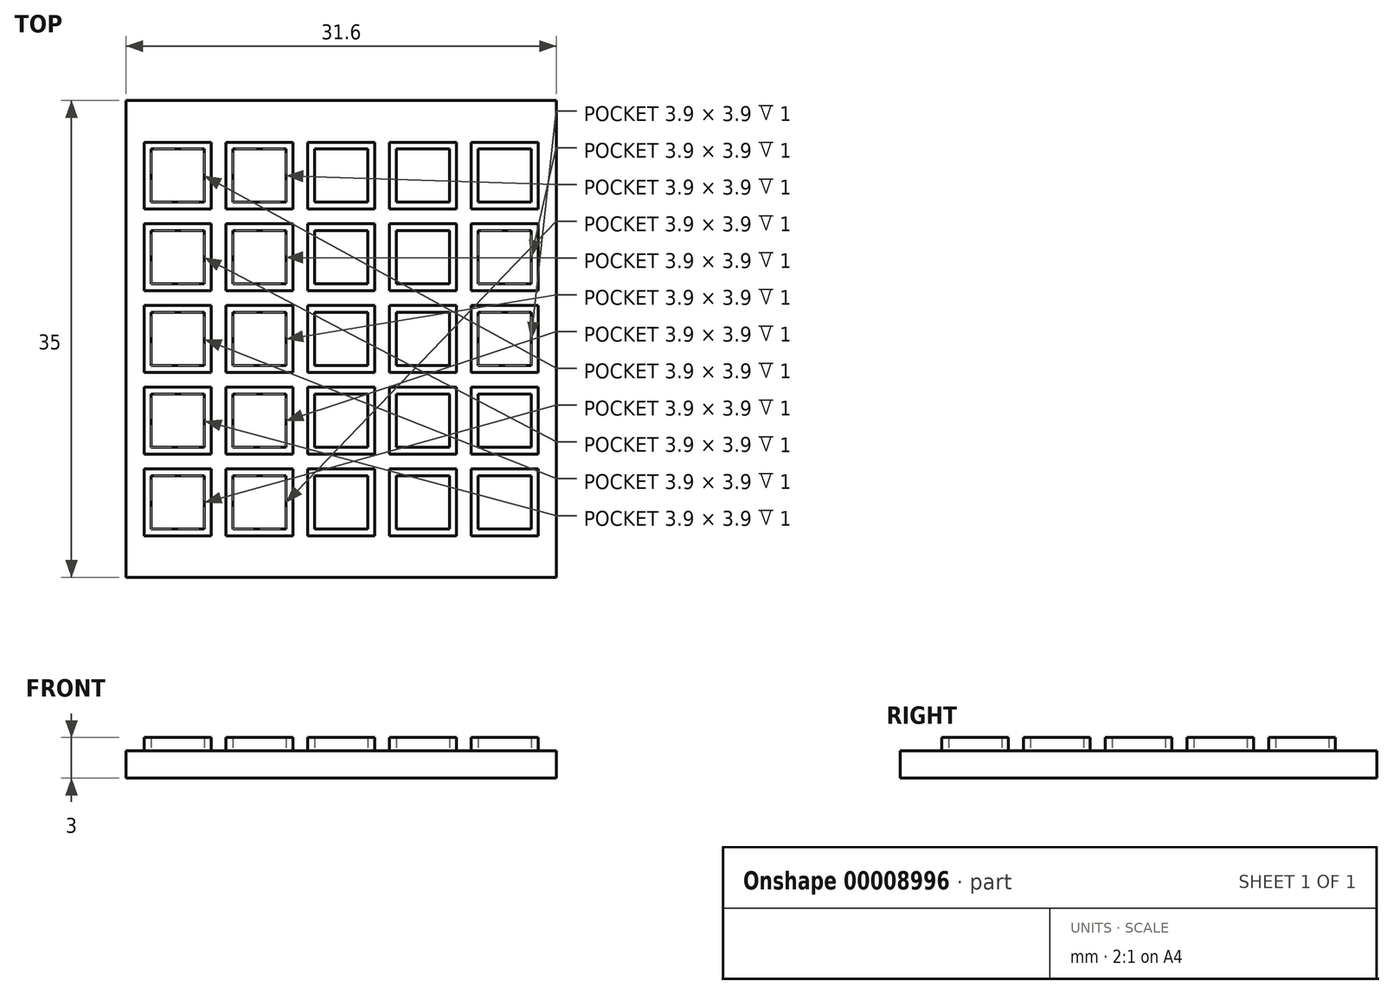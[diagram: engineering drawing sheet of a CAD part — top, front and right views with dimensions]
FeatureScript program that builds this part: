
annotation { "Feature Type Name" : "Feature", "Feature Type Description" : "" }
export const myFeature = defineFeature(function(context is Context, id is Id, definition is map)
    precondition{}
    {
        {
            var Q0;
            Q0=qCreatedBy(makeId("Top.planeOp"),FACE);
            var sketch = newSketch(context, id + "F0", { "sketchPlane" : qUnion([Q0])});
            skLineSegment(sketch, "E0.bottom", {"start": v(0, 0) * mm, "end": v(31.6, 0) * mm});
            skLineSegment(sketch, "E0.top", {"start": v(0, -35) * mm, "end": v(31.6, -35) * mm});
            skLineSegment(sketch, "E0.left", {"start": v(0, 0) * mm, "end": v(0, -35) * mm});
            skLineSegment(sketch, "E0.right", {"start": v(31.6, 0) * mm, "end": v(31.6, -35) * mm});
            skSolve(sketch);
        }
        {
            var Q0;
            Q0 = qSketchRegion(id + "F0", true);
            extrude(context, id + "F1", {"entities" : qUnion([Q0]), "depth" : 2 * mm});
        }
        {
            var Q0;
            Q0=makeQuery(id+"F1.opExtrude","CAP_FACE",FACE,{"disambiguationData":[OSD([sQuery(id+"F0.wireOp",EDGE,"E0.bottom"),sQuery(id+"F0.wireOp",EDGE,"E0.top"),sQuery(id+"F0.wireOp",EDGE,"E0.left"),sQuery(id+"F0.wireOp",EDGE,"E0.right")])],"isStart":false});
            var sketch = newSketch(context, id + "F2", { "sketchPlane" : qUnion([Q0])});
            skLineSegment(sketch, "E1", {"start": v(15.8, 0) * mm, "end": v(15.8, -35) * mm, "construction": true});
            skLineSegment(sketch, "E2.rect.bottom", {"start": v(18.25, -19.95) * mm, "end": v(13.35, -19.95) * mm});
            skLineSegment(sketch, "E2.rect.top", {"start": v(18.25, -15.05) * mm, "end": v(13.35, -15.05) * mm});
            skLineSegment(sketch, "E2.rect.left", {"start": v(18.25, -19.95) * mm, "end": v(18.25, -15.05) * mm});
            skLineSegment(sketch, "E2.rect.right", {"start": v(13.35, -19.95) * mm, "end": v(13.35, -15.05) * mm});
            skPoint(sketch, "E2.rect.middle", {"position": v(15.8, -17.5) * mm});
            skLineSegment(sketch, "E3.rect.bottom", {"start": v(17.75, -19.45) * mm, "end": v(13.85, -19.45) * mm});
            skLineSegment(sketch, "E3.rect.top", {"start": v(17.75, -15.55) * mm, "end": v(13.85, -15.55) * mm});
            skLineSegment(sketch, "E3.rect.left", {"start": v(17.75, -19.45) * mm, "end": v(17.75, -15.55) * mm});
            skLineSegment(sketch, "E3.rect.right", {"start": v(13.85, -19.45) * mm, "end": v(13.85, -15.55) * mm});
            skLineSegment(sketch, "E4.0.1.0", {"start": v(18.25, -13.95) * mm, "end": v(13.35, -13.95) * mm});
            skLineSegment(sketch, "E4.0.1.1", {"start": v(18.25, -9.05) * mm, "end": v(13.35, -9.05) * mm});
            skLineSegment(sketch, "E4.0.1.2", {"start": v(13.85, -13.45) * mm, "end": v(13.85, -9.55) * mm});
            skLineSegment(sketch, "E4.0.1.3", {"start": v(17.75, -13.45) * mm, "end": v(17.75, -9.55) * mm});
            skPoint(sketch, "E4.0.1.4", {"position": v(15.8, -11.5) * mm});
            skLineSegment(sketch, "E4.0.1.5", {"start": v(18.25, -13.95) * mm, "end": v(18.25, -9.05) * mm});
            skLineSegment(sketch, "E4.0.1.6", {"start": v(17.75, -9.55) * mm, "end": v(13.85, -9.55) * mm});
            skLineSegment(sketch, "E4.0.1.7", {"start": v(13.35, -13.95) * mm, "end": v(13.35, -9.05) * mm});
            skLineSegment(sketch, "E4.0.1.8", {"start": v(17.75, -13.45) * mm, "end": v(13.85, -13.45) * mm});
            skPoint(sketch, "E4.0.1.9", {"position": v(15.8, -11.5) * mm});
            skLineSegment(sketch, "E4.0.2.0", {"start": v(18.25, -7.95) * mm, "end": v(13.35, -7.95) * mm});
            skLineSegment(sketch, "E4.0.2.1", {"start": v(18.25, -3.05) * mm, "end": v(13.35, -3.05) * mm});
            skLineSegment(sketch, "E4.0.2.2", {"start": v(13.85, -7.45) * mm, "end": v(13.85, -3.55) * mm});
            skLineSegment(sketch, "E4.0.2.3", {"start": v(17.75, -7.45) * mm, "end": v(17.75, -3.55) * mm});
            skPoint(sketch, "E4.0.2.4", {"position": v(15.8, -5.5) * mm});
            skLineSegment(sketch, "E4.0.2.5", {"start": v(18.25, -7.95) * mm, "end": v(18.25, -3.05) * mm});
            skLineSegment(sketch, "E4.0.2.6", {"start": v(17.75, -3.55) * mm, "end": v(13.85, -3.55) * mm});
            skLineSegment(sketch, "E4.0.2.7", {"start": v(13.35, -7.95) * mm, "end": v(13.35, -3.05) * mm});
            skLineSegment(sketch, "E4.0.2.8", {"start": v(17.75, -7.45) * mm, "end": v(13.85, -7.45) * mm});
            skPoint(sketch, "E4.0.2.9", {"position": v(15.8, -5.5) * mm});
            skLineSegment(sketch, "E4.direction1", {"start": v(13.35, -19.95) * mm, "end": v(38.35, -19.95) * mm, "construction": true});
            skLineSegment(sketch, "E4.direction2", {"start": v(13.35, -19.95) * mm, "end": v(13.35, -13.95) * mm, "construction": true});
            skPoint(sketch, "E5.0.1.0", {"position": v(15.8, -23.5) * mm});
            skLineSegment(sketch, "E5.0.1.1", {"start": v(13.35, -25.95) * mm, "end": v(13.35, -21.05) * mm});
            skLineSegment(sketch, "E5.0.1.2", {"start": v(18.25, -25.95) * mm, "end": v(18.25, -21.05) * mm});
            skLineSegment(sketch, "E5.0.1.3", {"start": v(18.25, -25.95) * mm, "end": v(13.35, -25.95) * mm});
            skLineSegment(sketch, "E5.0.1.4", {"start": v(18.25, -21.05) * mm, "end": v(13.35, -21.05) * mm});
            skLineSegment(sketch, "E5.0.1.5", {"start": v(17.75, -25.45) * mm, "end": v(13.85, -25.45) * mm});
            skLineSegment(sketch, "E5.0.1.6", {"start": v(17.75, -21.55) * mm, "end": v(13.85, -21.55) * mm});
            skLineSegment(sketch, "E5.0.1.7", {"start": v(13.85, -25.45) * mm, "end": v(13.85, -21.55) * mm});
            skPoint(sketch, "E5.0.1.8", {"position": v(15.8, -23.5) * mm});
            skLineSegment(sketch, "E5.0.1.9", {"start": v(17.75, -25.45) * mm, "end": v(17.75, -21.55) * mm});
            skPoint(sketch, "E5.0.2.0", {"position": v(15.8, -29.5) * mm});
            skLineSegment(sketch, "E5.0.2.1", {"start": v(13.35, -31.95) * mm, "end": v(13.35, -27.05) * mm});
            skLineSegment(sketch, "E5.0.2.2", {"start": v(18.25, -31.95) * mm, "end": v(18.25, -27.05) * mm});
            skLineSegment(sketch, "E5.0.2.3", {"start": v(18.25, -31.95) * mm, "end": v(13.35, -31.95) * mm});
            skLineSegment(sketch, "E5.0.2.4", {"start": v(18.25, -27.05) * mm, "end": v(13.35, -27.05) * mm});
            skLineSegment(sketch, "E5.0.2.5", {"start": v(17.75, -31.45) * mm, "end": v(13.85, -31.45) * mm});
            skLineSegment(sketch, "E5.0.2.6", {"start": v(17.75, -27.55) * mm, "end": v(13.85, -27.55) * mm});
            skLineSegment(sketch, "E5.0.2.7", {"start": v(13.85, -31.45) * mm, "end": v(13.85, -27.55) * mm});
            skPoint(sketch, "E5.0.2.8", {"position": v(15.8, -29.5) * mm});
            skLineSegment(sketch, "E5.0.2.9", {"start": v(17.75, -31.45) * mm, "end": v(17.75, -27.55) * mm});
            skLineSegment(sketch, "E5.direction1", {"start": v(15.8, -17.5) * mm, "end": v(40.8, -17.5) * mm, "construction": true});
            skLineSegment(sketch, "E5.direction2", {"start": v(15.8, -17.5) * mm, "end": v(15.8, -23.5) * mm, "construction": true});
            skLineSegment(sketch, "E6.1.0.0", {"start": v(24.25, -31.95) * mm, "end": v(24.25, -27.05) * mm});
            skLineSegment(sketch, "E6.1.0.1", {"start": v(24.25, -25.95) * mm, "end": v(24.25, -21.05) * mm});
            skPoint(sketch, "E6.1.0.2", {"position": v(21.8, -11.5) * mm});
            skPoint(sketch, "E6.1.0.3", {"position": v(21.8, -5.5) * mm});
            skPoint(sketch, "E6.1.0.4", {"position": v(21.8, -29.5) * mm});
            skLineSegment(sketch, "E6.1.0.5", {"start": v(24.25, -7.95) * mm, "end": v(24.25, -3.05) * mm});
            skPoint(sketch, "E6.1.0.6", {"position": v(21.8, -23.5) * mm});
            skPoint(sketch, "E6.1.0.7", {"position": v(21.8, -17.5) * mm});
            skPoint(sketch, "E6.1.0.8", {"position": v(21.8, -5.5) * mm});
            skPoint(sketch, "E6.1.0.9", {"position": v(21.8, -17.5) * mm});
            skPoint(sketch, "E6.1.0.10", {"position": v(21.8, -29.5) * mm});
            skLineSegment(sketch, "E6.1.0.11", {"start": v(21.8, 0) * mm, "end": v(21.8, -35) * mm, "construction": true});
            skPoint(sketch, "E6.1.0.12", {"position": v(21.8, -11.5) * mm});
            skPoint(sketch, "E6.1.0.13", {"position": v(21.8, -23.5) * mm});
            skLineSegment(sketch, "E6.1.0.14", {"start": v(24.25, -25.95) * mm, "end": v(19.35, -25.95) * mm});
            skLineSegment(sketch, "E6.1.0.15", {"start": v(24.25, -31.95) * mm, "end": v(19.35, -31.95) * mm});
            skLineSegment(sketch, "E6.1.0.16", {"start": v(24.25, -7.95) * mm, "end": v(19.35, -7.95) * mm});
            skLineSegment(sketch, "E6.1.0.17", {"start": v(19.35, -31.95) * mm, "end": v(19.35, -27.05) * mm});
            skLineSegment(sketch, "E6.1.0.18", {"start": v(19.85, -7.45) * mm, "end": v(19.85, -3.55) * mm});
            skLineSegment(sketch, "E6.1.0.19", {"start": v(23.75, -31.45) * mm, "end": v(23.75, -27.55) * mm});
            skLineSegment(sketch, "E6.1.0.20", {"start": v(23.75, -7.45) * mm, "end": v(23.75, -3.55) * mm});
            skLineSegment(sketch, "E6.1.0.21", {"start": v(23.75, -25.45) * mm, "end": v(19.85, -25.45) * mm});
            skLineSegment(sketch, "E6.1.0.22", {"start": v(24.25, -3.05) * mm, "end": v(19.35, -3.05) * mm});
            skLineSegment(sketch, "E6.1.0.23", {"start": v(24.25, -19.95) * mm, "end": v(24.25, -15.05) * mm});
            skLineSegment(sketch, "E6.1.0.24", {"start": v(19.85, -31.45) * mm, "end": v(19.85, -27.55) * mm});
            skLineSegment(sketch, "E6.1.0.25", {"start": v(24.25, -27.05) * mm, "end": v(19.35, -27.05) * mm});
            skLineSegment(sketch, "E6.1.0.26", {"start": v(19.35, -7.95) * mm, "end": v(19.35, -3.05) * mm});
            skLineSegment(sketch, "E6.1.0.27", {"start": v(23.75, -31.45) * mm, "end": v(19.85, -31.45) * mm});
            skLineSegment(sketch, "E6.1.0.28", {"start": v(23.75, -3.55) * mm, "end": v(19.85, -3.55) * mm});
            skLineSegment(sketch, "E6.1.0.29", {"start": v(23.75, -27.55) * mm, "end": v(19.85, -27.55) * mm});
            skLineSegment(sketch, "E6.1.0.30", {"start": v(19.85, -25.45) * mm, "end": v(19.85, -21.55) * mm});
            skLineSegment(sketch, "E6.1.0.31", {"start": v(19.35, -25.95) * mm, "end": v(19.35, -21.05) * mm});
            skLineSegment(sketch, "E6.1.0.32", {"start": v(19.85, -13.45) * mm, "end": v(19.85, -9.55) * mm});
            skLineSegment(sketch, "E6.1.0.33", {"start": v(23.75, -13.45) * mm, "end": v(23.75, -9.55) * mm});
            skLineSegment(sketch, "E6.1.0.34", {"start": v(23.75, -19.45) * mm, "end": v(19.85, -19.45) * mm});
            skLineSegment(sketch, "E6.1.0.35", {"start": v(23.75, -15.55) * mm, "end": v(19.85, -15.55) * mm});
            skLineSegment(sketch, "E6.1.0.36", {"start": v(23.75, -19.45) * mm, "end": v(23.75, -15.55) * mm});
            skLineSegment(sketch, "E6.1.0.37", {"start": v(24.25, -9.05) * mm, "end": v(19.35, -9.05) * mm});
            skLineSegment(sketch, "E6.1.0.38", {"start": v(19.85, -19.45) * mm, "end": v(19.85, -15.55) * mm});
            skLineSegment(sketch, "E6.1.0.39", {"start": v(24.25, -13.95) * mm, "end": v(19.35, -13.95) * mm});
            skLineSegment(sketch, "E6.1.0.40", {"start": v(19.35, -19.95) * mm, "end": v(19.35, -15.05) * mm});
            skLineSegment(sketch, "E6.1.0.41", {"start": v(19.35, -19.95) * mm, "end": v(19.35, -13.95) * mm, "construction": true});
            skLineSegment(sketch, "E6.1.0.42", {"start": v(23.75, -25.45) * mm, "end": v(23.75, -21.55) * mm});
            skLineSegment(sketch, "E6.1.0.43", {"start": v(24.25, -19.95) * mm, "end": v(19.35, -19.95) * mm});
            skLineSegment(sketch, "E6.1.0.44", {"start": v(19.35, -13.95) * mm, "end": v(19.35, -9.05) * mm});
            skLineSegment(sketch, "E6.1.0.45", {"start": v(23.75, -9.55) * mm, "end": v(19.85, -9.55) * mm});
            skLineSegment(sketch, "E6.1.0.46", {"start": v(24.25, -13.95) * mm, "end": v(24.25, -9.05) * mm});
            skLineSegment(sketch, "E6.1.0.47", {"start": v(21.8, -17.5) * mm, "end": v(21.8, -23.5) * mm, "construction": true});
            skLineSegment(sketch, "E6.1.0.48", {"start": v(23.75, -21.55) * mm, "end": v(19.85, -21.55) * mm});
            skLineSegment(sketch, "E6.1.0.49", {"start": v(23.75, -13.45) * mm, "end": v(19.85, -13.45) * mm});
            skLineSegment(sketch, "E6.1.0.50", {"start": v(23.75, -7.45) * mm, "end": v(19.85, -7.45) * mm});
            skLineSegment(sketch, "E6.1.0.51", {"start": v(24.25, -21.05) * mm, "end": v(19.35, -21.05) * mm});
            skLineSegment(sketch, "E6.1.0.52", {"start": v(24.25, -15.05) * mm, "end": v(19.35, -15.05) * mm});
            skLineSegment(sketch, "E6.2.0.0", {"start": v(30.25, -31.95) * mm, "end": v(30.25, -27.05) * mm});
            skLineSegment(sketch, "E6.2.0.1", {"start": v(30.25, -25.95) * mm, "end": v(30.25, -21.05) * mm});
            skPoint(sketch, "E6.2.0.2", {"position": v(27.8, -11.5) * mm});
            skPoint(sketch, "E6.2.0.3", {"position": v(27.8, -5.5) * mm});
            skPoint(sketch, "E6.2.0.4", {"position": v(27.8, -29.5) * mm});
            skLineSegment(sketch, "E6.2.0.5", {"start": v(30.25, -7.95) * mm, "end": v(30.25, -3.05) * mm});
            skPoint(sketch, "E6.2.0.6", {"position": v(27.8, -23.5) * mm});
            skPoint(sketch, "E6.2.0.7", {"position": v(27.8, -17.5) * mm});
            skPoint(sketch, "E6.2.0.8", {"position": v(27.8, -5.5) * mm});
            skPoint(sketch, "E6.2.0.9", {"position": v(27.8, -17.5) * mm});
            skPoint(sketch, "E6.2.0.10", {"position": v(27.8, -29.5) * mm});
            skLineSegment(sketch, "E6.2.0.11", {"start": v(27.8, 0) * mm, "end": v(27.8, -35) * mm, "construction": true});
            skPoint(sketch, "E6.2.0.12", {"position": v(27.8, -11.5) * mm});
            skPoint(sketch, "E6.2.0.13", {"position": v(27.8, -23.5) * mm});
            skLineSegment(sketch, "E6.2.0.14", {"start": v(30.25, -25.95) * mm, "end": v(25.35, -25.95) * mm});
            skLineSegment(sketch, "E6.2.0.15", {"start": v(30.25, -31.95) * mm, "end": v(25.35, -31.95) * mm});
            skLineSegment(sketch, "E6.2.0.16", {"start": v(30.25, -7.95) * mm, "end": v(25.35, -7.95) * mm});
            skLineSegment(sketch, "E6.2.0.17", {"start": v(25.35, -31.95) * mm, "end": v(25.35, -27.05) * mm});
            skLineSegment(sketch, "E6.2.0.18", {"start": v(25.85, -7.45) * mm, "end": v(25.85, -3.55) * mm});
            skLineSegment(sketch, "E6.2.0.19", {"start": v(29.75, -31.45) * mm, "end": v(29.75, -27.55) * mm});
            skLineSegment(sketch, "E6.2.0.20", {"start": v(29.75, -7.45) * mm, "end": v(29.75, -3.55) * mm});
            skLineSegment(sketch, "E6.2.0.21", {"start": v(29.75, -25.45) * mm, "end": v(25.85, -25.45) * mm});
            skLineSegment(sketch, "E6.2.0.22", {"start": v(30.25, -3.05) * mm, "end": v(25.35, -3.05) * mm});
            skLineSegment(sketch, "E6.2.0.23", {"start": v(30.25, -19.95) * mm, "end": v(30.25, -15.05) * mm});
            skLineSegment(sketch, "E6.2.0.24", {"start": v(25.85, -31.45) * mm, "end": v(25.85, -27.55) * mm});
            skLineSegment(sketch, "E6.2.0.25", {"start": v(30.25, -27.05) * mm, "end": v(25.35, -27.05) * mm});
            skLineSegment(sketch, "E6.2.0.26", {"start": v(25.35, -7.95) * mm, "end": v(25.35, -3.05) * mm});
            skLineSegment(sketch, "E6.2.0.27", {"start": v(29.75, -31.45) * mm, "end": v(25.85, -31.45) * mm});
            skLineSegment(sketch, "E6.2.0.28", {"start": v(29.75, -3.55) * mm, "end": v(25.85, -3.55) * mm});
            skLineSegment(sketch, "E6.2.0.29", {"start": v(29.75, -27.55) * mm, "end": v(25.85, -27.55) * mm});
            skLineSegment(sketch, "E6.2.0.30", {"start": v(25.85, -25.45) * mm, "end": v(25.85, -21.55) * mm});
            skLineSegment(sketch, "E6.2.0.31", {"start": v(25.35, -25.95) * mm, "end": v(25.35, -21.05) * mm});
            skLineSegment(sketch, "E6.2.0.32", {"start": v(25.85, -13.45) * mm, "end": v(25.85, -9.55) * mm});
            skLineSegment(sketch, "E6.2.0.33", {"start": v(29.75, -13.45) * mm, "end": v(29.75, -9.55) * mm});
            skLineSegment(sketch, "E6.2.0.34", {"start": v(29.75, -19.45) * mm, "end": v(25.85, -19.45) * mm});
            skLineSegment(sketch, "E6.2.0.35", {"start": v(29.75, -15.55) * mm, "end": v(25.85, -15.55) * mm});
            skLineSegment(sketch, "E6.2.0.36", {"start": v(29.75, -19.45) * mm, "end": v(29.75, -15.55) * mm});
            skLineSegment(sketch, "E6.2.0.37", {"start": v(30.25, -9.05) * mm, "end": v(25.35, -9.05) * mm});
            skLineSegment(sketch, "E6.2.0.38", {"start": v(25.85, -19.45) * mm, "end": v(25.85, -15.55) * mm});
            skLineSegment(sketch, "E6.2.0.39", {"start": v(30.25, -13.95) * mm, "end": v(25.35, -13.95) * mm});
            skLineSegment(sketch, "E6.2.0.40", {"start": v(25.35, -19.95) * mm, "end": v(25.35, -15.05) * mm});
            skLineSegment(sketch, "E6.2.0.41", {"start": v(25.35, -19.95) * mm, "end": v(25.35, -13.95) * mm, "construction": true});
            skLineSegment(sketch, "E6.2.0.42", {"start": v(29.75, -25.45) * mm, "end": v(29.75, -21.55) * mm});
            skLineSegment(sketch, "E6.2.0.43", {"start": v(30.25, -19.95) * mm, "end": v(25.35, -19.95) * mm});
            skLineSegment(sketch, "E6.2.0.44", {"start": v(25.35, -13.95) * mm, "end": v(25.35, -9.05) * mm});
            skLineSegment(sketch, "E6.2.0.45", {"start": v(29.75, -9.55) * mm, "end": v(25.85, -9.55) * mm});
            skLineSegment(sketch, "E6.2.0.46", {"start": v(30.25, -13.95) * mm, "end": v(30.25, -9.05) * mm});
            skLineSegment(sketch, "E6.2.0.47", {"start": v(27.8, -17.5) * mm, "end": v(27.8, -23.5) * mm, "construction": true});
            skLineSegment(sketch, "E6.2.0.48", {"start": v(29.75, -21.55) * mm, "end": v(25.85, -21.55) * mm});
            skLineSegment(sketch, "E6.2.0.49", {"start": v(29.75, -13.45) * mm, "end": v(25.85, -13.45) * mm});
            skLineSegment(sketch, "E6.2.0.50", {"start": v(29.75, -7.45) * mm, "end": v(25.85, -7.45) * mm});
            skLineSegment(sketch, "E6.2.0.51", {"start": v(30.25, -21.05) * mm, "end": v(25.35, -21.05) * mm});
            skLineSegment(sketch, "E6.2.0.52", {"start": v(30.25, -15.05) * mm, "end": v(25.35, -15.05) * mm});
            skLineSegment(sketch, "E6.direction1", {"start": v(18.25, -31.95) * mm, "end": v(24.25, -31.95) * mm, "construction": true});
            skPoint(sketch, "E7.1.0.0", {"position": v(9.8, -5.5) * mm});
            skLineSegment(sketch, "E7.1.0.1", {"start": v(7.35, -7.95) * mm, "end": v(7.35, -3.05) * mm});
            skLineSegment(sketch, "E7.1.0.2", {"start": v(12.25, -31.95) * mm, "end": v(12.25, -27.05) * mm});
            skPoint(sketch, "E7.1.0.3", {"position": v(9.8, -11.5) * mm});
            skPoint(sketch, "E7.1.0.4", {"position": v(9.8, -17.5) * mm});
            skPoint(sketch, "E7.1.0.5", {"position": v(9.8, -17.5) * mm});
            skLineSegment(sketch, "E7.1.0.6", {"start": v(12.25, -27.05) * mm, "end": v(7.35, -27.05) * mm});
            skLineSegment(sketch, "E7.1.0.7", {"start": v(12.25, -31.95) * mm, "end": v(7.35, -31.95) * mm});
            skLineSegment(sketch, "E7.1.0.8", {"start": v(12.25, -7.95) * mm, "end": v(12.25, -3.05) * mm});
            skLineSegment(sketch, "E7.1.0.9", {"start": v(12.25, -3.05) * mm, "end": v(7.35, -3.05) * mm});
            skLineSegment(sketch, "E7.1.0.10", {"start": v(12.25, -9.05) * mm, "end": v(7.35, -9.05) * mm});
            skLineSegment(sketch, "E7.1.0.11", {"start": v(12.25, -13.95) * mm, "end": v(7.35, -13.95) * mm});
            skLineSegment(sketch, "E7.1.0.12", {"start": v(7.85, -7.45) * mm, "end": v(7.85, -3.55) * mm});
            skLineSegment(sketch, "E7.1.0.13", {"start": v(7.35, -31.95) * mm, "end": v(7.35, -27.05) * mm});
            skLineSegment(sketch, "E7.1.0.14", {"start": v(12.25, -13.95) * mm, "end": v(12.25, -9.05) * mm});
            skLineSegment(sketch, "E7.1.0.15", {"start": v(11.75, -9.55) * mm, "end": v(7.85, -9.55) * mm});
            skLineSegment(sketch, "E7.1.0.16", {"start": v(7.35, -13.95) * mm, "end": v(7.35, -9.05) * mm});
            skLineSegment(sketch, "E7.1.0.17", {"start": v(9.8, 0) * mm, "end": v(9.8, -35) * mm, "construction": true});
            skLineSegment(sketch, "E7.1.0.18", {"start": v(12.25, -19.95) * mm, "end": v(7.35, -19.95) * mm});
            skLineSegment(sketch, "E7.1.0.19", {"start": v(12.25, -15.05) * mm, "end": v(7.35, -15.05) * mm});
            skLineSegment(sketch, "E7.1.0.20", {"start": v(12.25, -19.95) * mm, "end": v(12.25, -15.05) * mm});
            skLineSegment(sketch, "E7.1.0.21", {"start": v(7.35, -19.95) * mm, "end": v(7.35, -15.05) * mm});
            skLineSegment(sketch, "E7.1.0.22", {"start": v(11.75, -19.45) * mm, "end": v(7.85, -19.45) * mm});
            skLineSegment(sketch, "E7.1.0.23", {"start": v(11.75, -15.55) * mm, "end": v(7.85, -15.55) * mm});
            skLineSegment(sketch, "E7.1.0.24", {"start": v(11.75, -13.45) * mm, "end": v(7.85, -13.45) * mm});
            skPoint(sketch, "E7.1.0.25", {"position": v(9.8, -29.5) * mm});
            skLineSegment(sketch, "E7.1.0.26", {"start": v(12.25, -7.95) * mm, "end": v(7.35, -7.95) * mm});
            skPoint(sketch, "E7.1.0.27", {"position": v(9.8, -29.5) * mm});
            skPoint(sketch, "E7.1.0.28", {"position": v(9.8, -23.5) * mm});
            skLineSegment(sketch, "E7.1.0.29", {"start": v(9.8, -17.5) * mm, "end": v(9.8, -23.5) * mm, "construction": true});
            skLineSegment(sketch, "E7.1.0.30", {"start": v(12.25, -25.95) * mm, "end": v(12.25, -21.05) * mm});
            skPoint(sketch, "E7.1.0.31", {"position": v(9.8, -5.5) * mm});
            skLineSegment(sketch, "E7.1.0.32", {"start": v(12.25, -25.95) * mm, "end": v(7.35, -25.95) * mm});
            skPoint(sketch, "E7.1.0.33", {"position": v(9.8, -23.5) * mm});
            skLineSegment(sketch, "E7.1.0.34", {"start": v(7.35, -25.95) * mm, "end": v(7.35, -21.05) * mm});
            skLineSegment(sketch, "E7.1.0.35", {"start": v(12.25, -21.05) * mm, "end": v(7.35, -21.05) * mm});
            skPoint(sketch, "E7.1.0.36", {"position": v(9.8, -11.5) * mm});
            skLineSegment(sketch, "E7.1.0.37", {"start": v(7.35, -19.95) * mm, "end": v(7.35, -13.95) * mm, "construction": true});
            skLineSegment(sketch, "E7.1.0.38", {"start": v(11.75, -31.45) * mm, "end": v(11.75, -27.55) * mm});
            skLineSegment(sketch, "E7.1.0.39", {"start": v(11.75, -7.45) * mm, "end": v(7.85, -7.45) * mm});
            skLineSegment(sketch, "E7.1.0.40", {"start": v(11.75, -27.55) * mm, "end": v(7.85, -27.55) * mm});
            skLineSegment(sketch, "E7.1.0.41", {"start": v(11.75, -31.45) * mm, "end": v(7.85, -31.45) * mm});
            skLineSegment(sketch, "E7.1.0.42", {"start": v(7.85, -31.45) * mm, "end": v(7.85, -27.55) * mm});
            skLineSegment(sketch, "E7.1.0.43", {"start": v(11.75, -7.45) * mm, "end": v(11.75, -3.55) * mm});
            skLineSegment(sketch, "E7.1.0.44", {"start": v(11.75, -3.55) * mm, "end": v(7.85, -3.55) * mm});
            skLineSegment(sketch, "E7.1.0.45", {"start": v(11.75, -25.45) * mm, "end": v(11.75, -21.55) * mm});
            skLineSegment(sketch, "E7.1.0.46", {"start": v(11.75, -13.45) * mm, "end": v(11.75, -9.55) * mm});
            skLineSegment(sketch, "E7.1.0.47", {"start": v(7.85, -13.45) * mm, "end": v(7.85, -9.55) * mm});
            skLineSegment(sketch, "E7.1.0.48", {"start": v(7.85, -19.45) * mm, "end": v(7.85, -15.55) * mm});
            skLineSegment(sketch, "E7.1.0.49", {"start": v(11.75, -19.45) * mm, "end": v(11.75, -15.55) * mm});
            skLineSegment(sketch, "E7.1.0.50", {"start": v(11.75, -21.55) * mm, "end": v(7.85, -21.55) * mm});
            skLineSegment(sketch, "E7.1.0.51", {"start": v(7.85, -25.45) * mm, "end": v(7.85, -21.55) * mm});
            skLineSegment(sketch, "E7.1.0.52", {"start": v(11.75, -25.45) * mm, "end": v(7.85, -25.45) * mm});
            skPoint(sketch, "E7.2.0.0", {"position": v(3.8, -5.5) * mm});
            skLineSegment(sketch, "E7.2.0.1", {"start": v(1.35, -7.95) * mm, "end": v(1.35, -3.05) * mm});
            skLineSegment(sketch, "E7.2.0.2", {"start": v(6.25, -31.95) * mm, "end": v(6.25, -27.05) * mm});
            skPoint(sketch, "E7.2.0.3", {"position": v(3.8, -11.5) * mm});
            skPoint(sketch, "E7.2.0.4", {"position": v(3.8, -17.5) * mm});
            skPoint(sketch, "E7.2.0.5", {"position": v(3.8, -17.5) * mm});
            skLineSegment(sketch, "E7.2.0.6", {"start": v(6.25, -27.05) * mm, "end": v(1.35, -27.05) * mm});
            skLineSegment(sketch, "E7.2.0.7", {"start": v(6.25, -31.95) * mm, "end": v(1.35, -31.95) * mm});
            skLineSegment(sketch, "E7.2.0.8", {"start": v(6.25, -7.95) * mm, "end": v(6.25, -3.05) * mm});
            skLineSegment(sketch, "E7.2.0.9", {"start": v(6.25, -3.05) * mm, "end": v(1.35, -3.05) * mm});
            skLineSegment(sketch, "E7.2.0.10", {"start": v(6.25, -9.05) * mm, "end": v(1.35, -9.05) * mm});
            skLineSegment(sketch, "E7.2.0.11", {"start": v(6.25, -13.95) * mm, "end": v(1.35, -13.95) * mm});
            skLineSegment(sketch, "E7.2.0.12", {"start": v(1.85, -7.45) * mm, "end": v(1.85, -3.55) * mm});
            skLineSegment(sketch, "E7.2.0.13", {"start": v(1.35, -31.95) * mm, "end": v(1.35, -27.05) * mm});
            skLineSegment(sketch, "E7.2.0.14", {"start": v(6.25, -13.95) * mm, "end": v(6.25, -9.05) * mm});
            skLineSegment(sketch, "E7.2.0.15", {"start": v(5.75, -9.55) * mm, "end": v(1.85, -9.55) * mm});
            skLineSegment(sketch, "E7.2.0.16", {"start": v(1.35, -13.95) * mm, "end": v(1.35, -9.05) * mm});
            skLineSegment(sketch, "E7.2.0.17", {"start": v(3.8, 0) * mm, "end": v(3.8, -35) * mm, "construction": true});
            skLineSegment(sketch, "E7.2.0.18", {"start": v(6.25, -19.95) * mm, "end": v(1.35, -19.95) * mm});
            skLineSegment(sketch, "E7.2.0.19", {"start": v(6.25, -15.05) * mm, "end": v(1.35, -15.05) * mm});
            skLineSegment(sketch, "E7.2.0.20", {"start": v(6.25, -19.95) * mm, "end": v(6.25, -15.05) * mm});
            skLineSegment(sketch, "E7.2.0.21", {"start": v(1.35, -19.95) * mm, "end": v(1.35, -15.05) * mm});
            skLineSegment(sketch, "E7.2.0.22", {"start": v(5.75, -19.45) * mm, "end": v(1.85, -19.45) * mm});
            skLineSegment(sketch, "E7.2.0.23", {"start": v(5.75, -15.55) * mm, "end": v(1.85, -15.55) * mm});
            skLineSegment(sketch, "E7.2.0.24", {"start": v(5.75, -13.45) * mm, "end": v(1.85, -13.45) * mm});
            skPoint(sketch, "E7.2.0.25", {"position": v(3.8, -29.5) * mm});
            skLineSegment(sketch, "E7.2.0.26", {"start": v(6.25, -7.95) * mm, "end": v(1.35, -7.95) * mm});
            skPoint(sketch, "E7.2.0.27", {"position": v(3.8, -29.5) * mm});
            skPoint(sketch, "E7.2.0.28", {"position": v(3.8, -23.5) * mm});
            skLineSegment(sketch, "E7.2.0.29", {"start": v(3.8, -17.5) * mm, "end": v(3.8, -23.5) * mm, "construction": true});
            skLineSegment(sketch, "E7.2.0.30", {"start": v(6.25, -25.95) * mm, "end": v(6.25, -21.05) * mm});
            skPoint(sketch, "E7.2.0.31", {"position": v(3.8, -5.5) * mm});
            skLineSegment(sketch, "E7.2.0.32", {"start": v(6.25, -25.95) * mm, "end": v(1.35, -25.95) * mm});
            skPoint(sketch, "E7.2.0.33", {"position": v(3.8, -23.5) * mm});
            skLineSegment(sketch, "E7.2.0.34", {"start": v(1.35, -25.95) * mm, "end": v(1.35, -21.05) * mm});
            skLineSegment(sketch, "E7.2.0.35", {"start": v(6.25, -21.05) * mm, "end": v(1.35, -21.05) * mm});
            skPoint(sketch, "E7.2.0.36", {"position": v(3.8, -11.5) * mm});
            skLineSegment(sketch, "E7.2.0.37", {"start": v(1.35, -19.95) * mm, "end": v(1.35, -13.95) * mm, "construction": true});
            skLineSegment(sketch, "E7.2.0.38", {"start": v(5.75, -31.45) * mm, "end": v(5.75, -27.55) * mm});
            skLineSegment(sketch, "E7.2.0.39", {"start": v(5.75, -7.45) * mm, "end": v(1.85, -7.45) * mm});
            skLineSegment(sketch, "E7.2.0.40", {"start": v(5.75, -27.55) * mm, "end": v(1.85, -27.55) * mm});
            skLineSegment(sketch, "E7.2.0.41", {"start": v(5.75, -31.45) * mm, "end": v(1.85, -31.45) * mm});
            skLineSegment(sketch, "E7.2.0.42", {"start": v(1.85, -31.45) * mm, "end": v(1.85, -27.55) * mm});
            skLineSegment(sketch, "E7.2.0.43", {"start": v(5.75, -7.45) * mm, "end": v(5.75, -3.55) * mm});
            skLineSegment(sketch, "E7.2.0.44", {"start": v(5.75, -3.55) * mm, "end": v(1.85, -3.55) * mm});
            skLineSegment(sketch, "E7.2.0.45", {"start": v(5.75, -25.45) * mm, "end": v(5.75, -21.55) * mm});
            skLineSegment(sketch, "E7.2.0.46", {"start": v(5.75, -13.45) * mm, "end": v(5.75, -9.55) * mm});
            skLineSegment(sketch, "E7.2.0.47", {"start": v(1.85, -13.45) * mm, "end": v(1.85, -9.55) * mm});
            skLineSegment(sketch, "E7.2.0.48", {"start": v(1.85, -19.45) * mm, "end": v(1.85, -15.55) * mm});
            skLineSegment(sketch, "E7.2.0.49", {"start": v(5.75, -19.45) * mm, "end": v(5.75, -15.55) * mm});
            skLineSegment(sketch, "E7.2.0.50", {"start": v(5.75, -21.55) * mm, "end": v(1.85, -21.55) * mm});
            skLineSegment(sketch, "E7.2.0.51", {"start": v(1.85, -25.45) * mm, "end": v(1.85, -21.55) * mm});
            skLineSegment(sketch, "E7.2.0.52", {"start": v(5.75, -25.45) * mm, "end": v(1.85, -25.45) * mm});
            skLineSegment(sketch, "E7.direction1", {"start": v(15.8, -5.5) * mm, "end": v(9.8, -5.5) * mm, "construction": true});
            skSolve(sketch);
        }
        {
            var Q0;
            Q0 = qSketchRegion(id + "F2", true);
            extrude(context, id + "F3", {"entities" : qUnion([Q0]), "operationType" : NewBodyOperationType.ADD, "depth" : 1 * mm});
        }
    });
